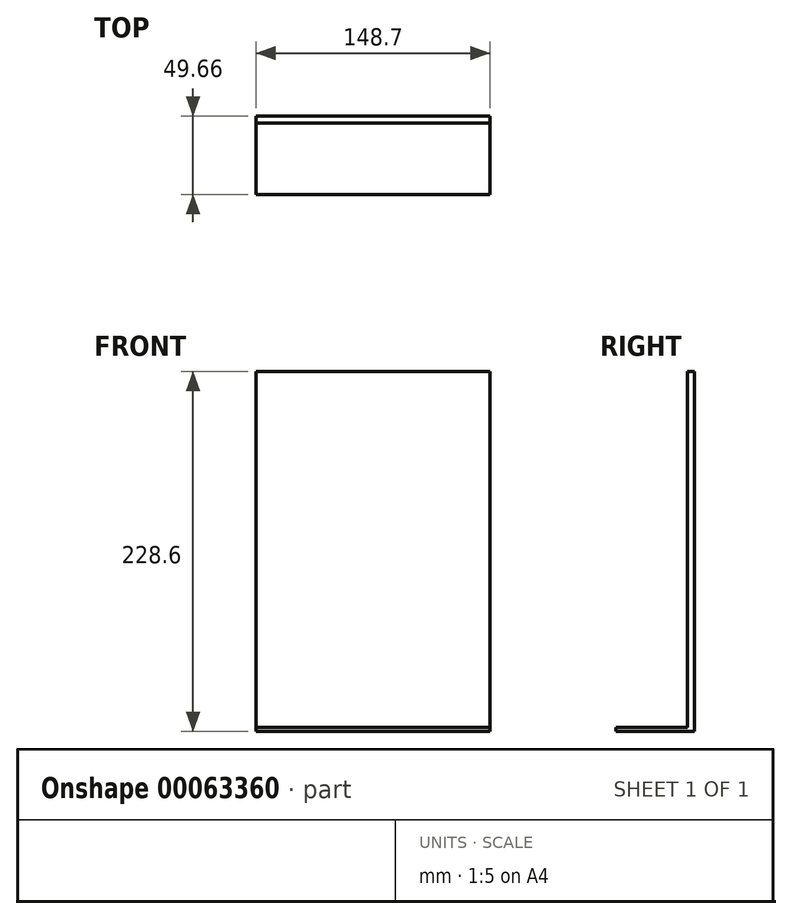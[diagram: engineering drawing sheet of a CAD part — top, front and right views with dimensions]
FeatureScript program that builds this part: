
annotation { "Feature Type Name" : "Feature", "Feature Type Description" : "" }
export const myFeature = defineFeature(function(context is Context, id is Id, definition is map)
    precondition{}
    {
        {
            var Q0;
            Q0=qCreatedBy(makeId("Top.planeOp"),FACE);
            var sketch = newSketch(context, id + "F0", { "sketchPlane" : qUnion([Q0])});
            skLineSegment(sketch, "E0.rect.bottom", {"start": v(74.35, -24.83) * mm, "end": v(-74.35, -24.83) * mm});
            skLineSegment(sketch, "E0.rect.top", {"start": v(74.35, 24.83) * mm, "end": v(-74.35, 24.83) * mm});
            skLineSegment(sketch, "E0.rect.left", {"start": v(74.35, -24.83) * mm, "end": v(74.35, 24.83) * mm});
            skLineSegment(sketch, "E0.rect.right", {"start": v(-74.35, -24.83) * mm, "end": v(-74.35, 24.83) * mm});
            skPoint(sketch, "E0.rect.middle", {"position": v(0, 0) * mm});
            skLineSegment(sketch, "E1", {"start": v(-74.35, 20.47) * mm, "end": v(74.35, 20.47) * mm});
            skLineSegment(sketch, "E2", {"start": v(-67.67, 20.47) * mm, "end": v(-67.67, -24.83) * mm});
            skLineSegment(sketch, "E3", {"start": v(65.92, 20.47) * mm, "end": v(65.92, -24.83) * mm});
            skLineSegment(sketch, "E4", {"start": v(-67.67, -20.47) * mm, "end": v(65.92, -20.47) * mm});
            skLineSegment(sketch, "E5", {"start": v(-49.95, 20.47) * mm, "end": v(-49.95, -20.47) * mm});
            skLineSegment(sketch, "E6", {"start": v(-52.86, 20.47) * mm, "end": v(-52.86, -20.47) * mm});
            skLineSegment(sketch, "E7", {"start": v(-25.27, 20.47) * mm, "end": v(-25.27, -20.47) * mm});
            skLineSegment(sketch, "E8", {"start": v(-20.91, 20.47) * mm, "end": v(-20.91, -20.47) * mm});
            skLineSegment(sketch, "E9", {"start": v(3.49, 20.47) * mm, "end": v(3.49, -20.47) * mm});
            skLineSegment(sketch, "E10", {"start": v(10.16, 20.47) * mm, "end": v(10.16, -20.47) * mm});
            skSolve(sketch);
        }
        {
            var Q0;
            {var subQ10=sQuery(id+"F0.wireOp",EDGE,"E0.rect.top");Q0=makeQuery(id+"F0.imprint","IMPRINT",FACE,{"disambiguationData":[TD([[makeQuery(id+"F0.imprint","IMPRINT",EDGE,{"derivedFrom":subQ10}),1.0]])]});}
            extrude(context, id + "F1", {"entities" : qUnion([Q0]), "depth" : 228.6 * mm});
        }
        {
            var Q0;
            Q0 = qSketchRegion(id + "F0", true);
            var Q1;
            {var subQ3=sQuery(id+"F0.wireOp",EDGE,"E6");Q1=makeQuery(id+"F0.imprint","IMPRINT",FACE,{"disambiguationData":[TD([[makeQuery(id+"F0.imprint","IMPRINT",EDGE,{"derivedFrom":subQ3}),-1.0]])]});}
            var Q2;
            {var subQ0=sQuery(id+"F0.wireOp",EDGE,"E5");Q2=makeQuery(id+"F0.imprint","IMPRINT",FACE,{"disambiguationData":[TD([[makeQuery(id+"F0.imprint","IMPRINT",EDGE,{"derivedFrom":subQ0}),-1.0]])]});}
            var Q3;
            {var subQ0=sQuery(id+"F0.wireOp",EDGE,"E5");Q3=makeQuery(id+"F0.imprint","IMPRINT",FACE,{"disambiguationData":[TD([[makeQuery(id+"F0.imprint","IMPRINT",EDGE,{"derivedFrom":subQ0}),1.0]])]});}
            var Q4;
            {var subQ0=sQuery(id+"F0.wireOp",EDGE,"E7");Q4=makeQuery(id+"F0.imprint","IMPRINT",FACE,{"disambiguationData":[TD([[makeQuery(id+"F0.imprint","IMPRINT",EDGE,{"derivedFrom":subQ0}),1.0]])]});}
            var Q5;
            {var subQ0=sQuery(id+"F0.wireOp",EDGE,"E8");Q5=makeQuery(id+"F0.imprint","IMPRINT",FACE,{"disambiguationData":[TD([[makeQuery(id+"F0.imprint","IMPRINT",EDGE,{"derivedFrom":subQ0}),1.0]])]});}
            var Q6;
            {var subQ0=sQuery(id+"F0.wireOp",EDGE,"E9");Q6=makeQuery(id+"F0.imprint","IMPRINT",FACE,{"disambiguationData":[TD([[makeQuery(id+"F0.imprint","IMPRINT",EDGE,{"derivedFrom":subQ0}),1.0]])]});}
            var Q7;
            {var subQ3=sQuery(id+"F0.wireOp",EDGE,"E10");Q7=makeQuery(id+"F0.imprint","IMPRINT",FACE,{"disambiguationData":[TD([[makeQuery(id+"F0.imprint","IMPRINT",EDGE,{"derivedFrom":subQ3}),1.0]])]});}
            extrude(context, id + "F2", {"entities" : qUnion([Q0, Q1, Q2, Q3, Q4, Q5, Q6, Q7]), "operationType" : NewBodyOperationType.ADD, "depth" : 2.54 * mm});
        }
    });
